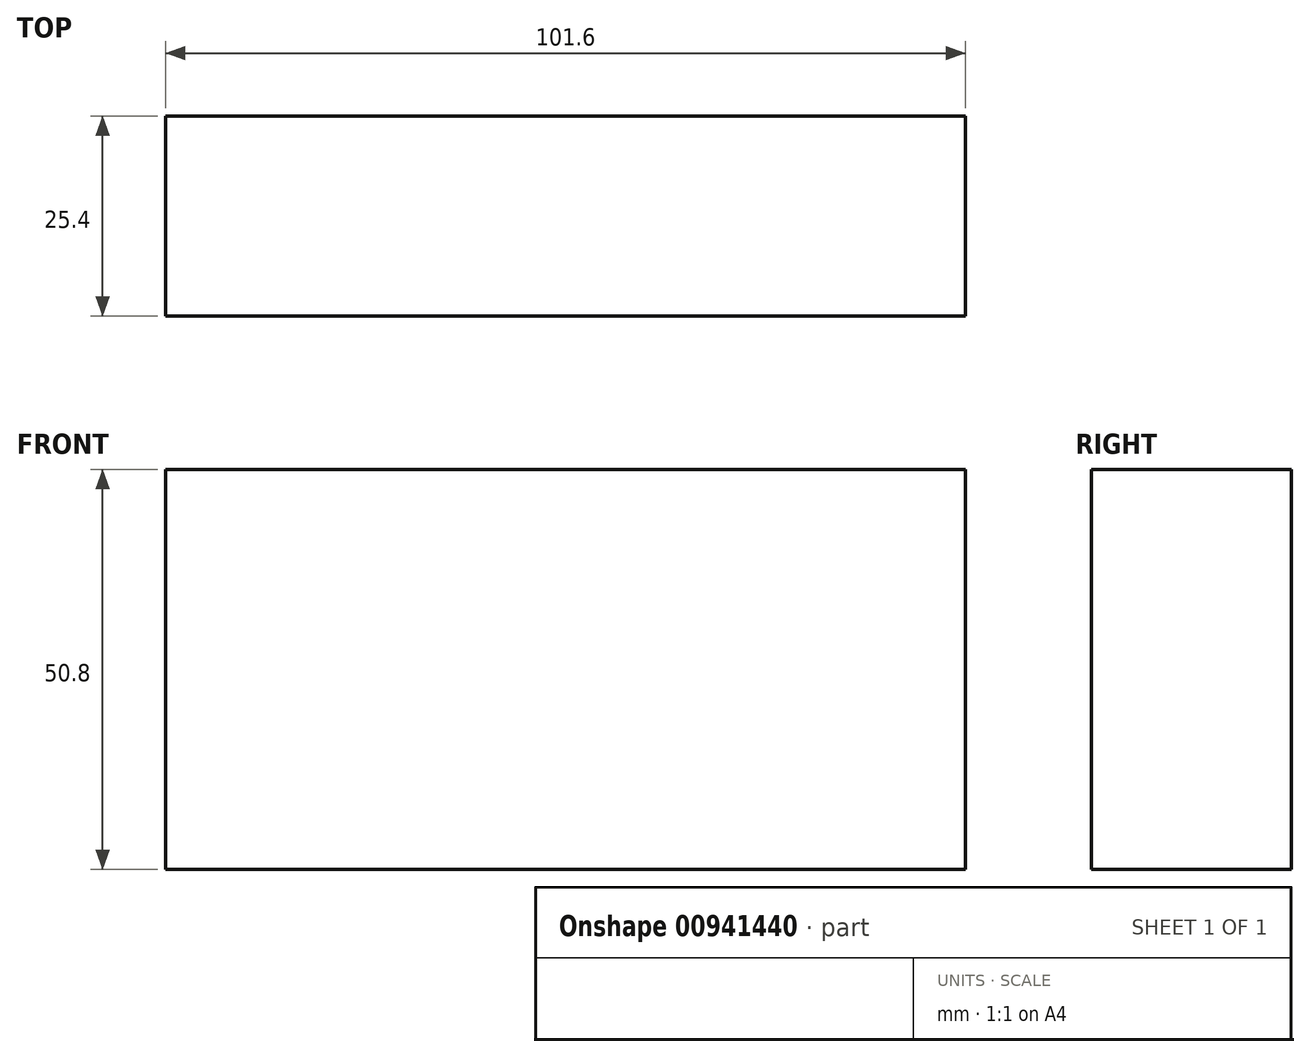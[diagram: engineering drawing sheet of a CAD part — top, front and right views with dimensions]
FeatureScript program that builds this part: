
annotation { "Feature Type Name" : "Feature", "Feature Type Description" : "" }
export const myFeature = defineFeature(function(context is Context, id is Id, definition is map)
    precondition{}
    {
        {
            var Q0;
            Q0=qCreatedBy(makeId("Front.planeOp"),FACE);
            var sketch = newSketch(context, id + "F0", { "sketchPlane" : qUnion([Q0])});
            skLineSegment(sketch, "E0", {"start": v(-52.58, 14.84) * mm, "end": v(49.02, 14.84) * mm});
            skLineSegment(sketch, "E1", {"start": v(49.02, 14.84) * mm, "end": v(49.02, -35.96) * mm});
            skLineSegment(sketch, "E2", {"start": v(49.02, -35.96) * mm, "end": v(-52.58, -35.96) * mm});
            skLineSegment(sketch, "E3", {"start": v(-52.58, -35.96) * mm, "end": v(-52.58, 14.84) * mm});
            skSolve(sketch);
        }
        {
            var Q0;
            Q0 = qSketchRegion(id + "F0", true);
            extrude(context, id + "F1", {"entities" : qUnion([Q0]), "depth" : 25.4 * mm, "offsetDistance" : 25.4 * mm});
        }
    });
